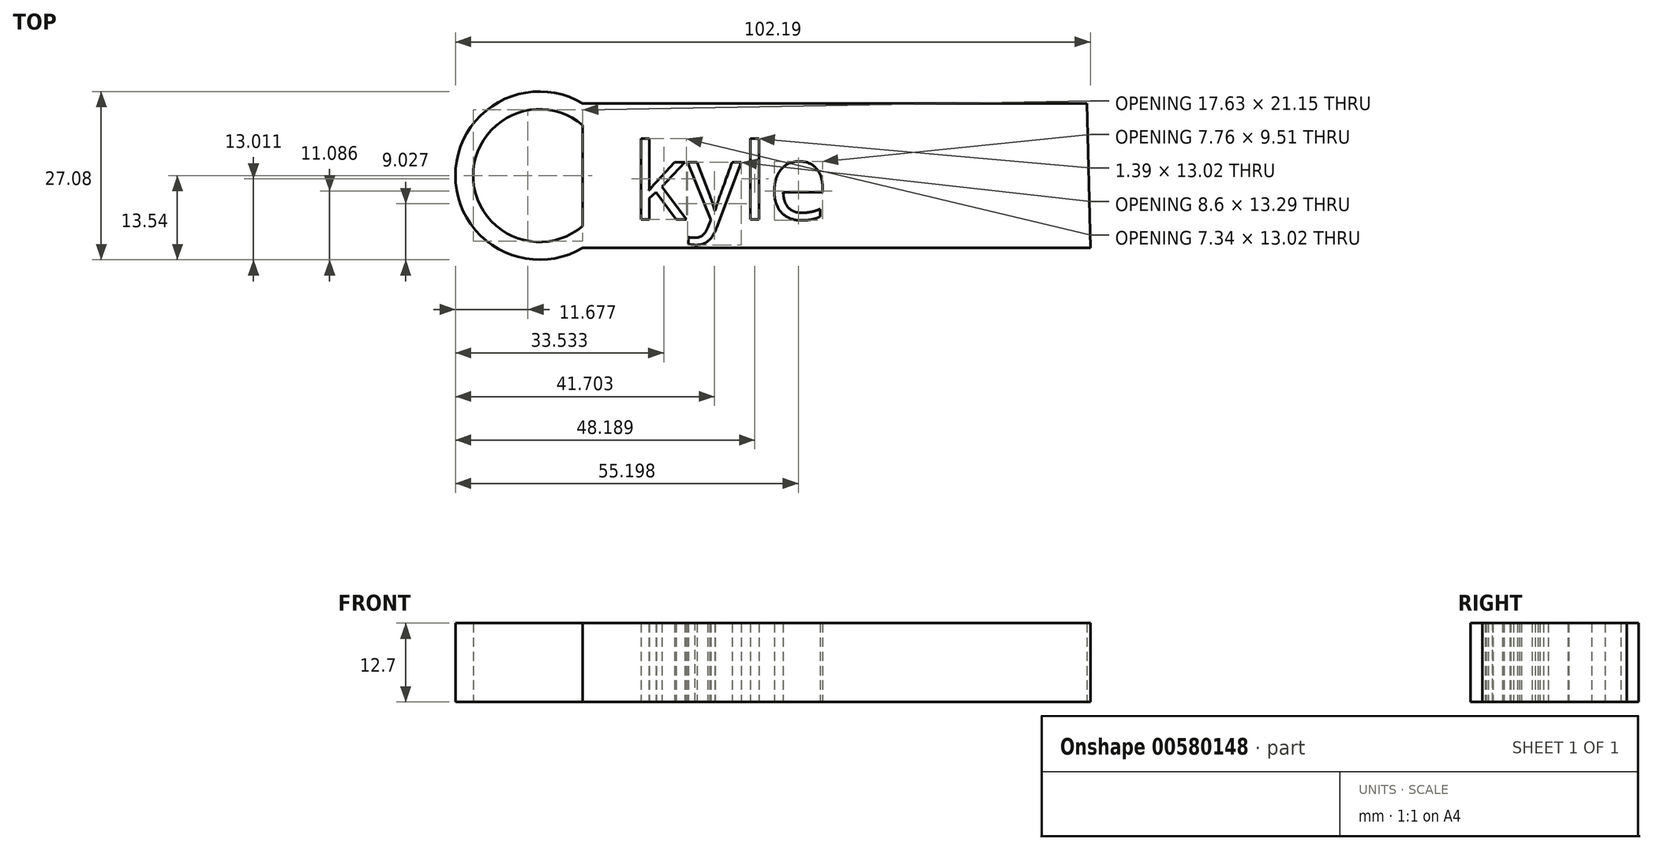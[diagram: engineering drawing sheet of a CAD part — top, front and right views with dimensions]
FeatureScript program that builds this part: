
annotation { "Feature Type Name" : "Feature", "Feature Type Description" : "" }
export const myFeature = defineFeature(function(context is Context, id is Id, definition is map)
    precondition{}
    {
        {
            var Q0;
            Q0=qCreatedBy(makeId("Top.planeOp"),FACE);
            var sketch = newSketch(context, id + "F0", { "sketchPlane" : qUnion([Q0])});
            skArc(sketch, "E0", {"start": v(-43.13, 11.62) * mm, "mid": v(-63.62, 0) * mm, "end": v(-43.13, -11.62) * mm});
            skArc(sketch, "E1", {"start": v(-43.13, 8.1) * mm, "mid": v(-60.76, 0) * mm, "end": v(-43.13, -8.1) * mm});
            skLineSegment(sketch, "E2", {"start": v(-43.13, 11.62) * mm, "end": v(38, 11.62) * mm});
            skLineSegment(sketch, "E3", {"start": v(-43.13, -11.62) * mm, "end": v(38.57, -11.62) * mm});
            skLineSegment(sketch, "E4", {"start": v(38, 11.62) * mm, "end": v(38.57, -11.62) * mm});
            skLineSegment(sketch, "E5", {"start": v(-43.13, 11.62) * mm, "end": v(-43.13, -11.62) * mm});
            skText(sketch, "E6", { "text": "kyle\n", "fontName": "OpenSans-Regular.ttf"});
            const initialGuessF0  = {"E6": [-0.03523, -0.00704, 1, 0, 0.01234]};
            skSetInitialGuess(sketch, initialGuessF0);
            skSolve(sketch);
        }
        {
            var Q0;
            Q0 = qSketchRegion(id + "F0", true);
            extrude(context, id + "F1", {"entities" : qUnion([Q0]), "depth" : 12.7 * mm, "offsetDistance" : 25.4 * mm});
        }
    });
